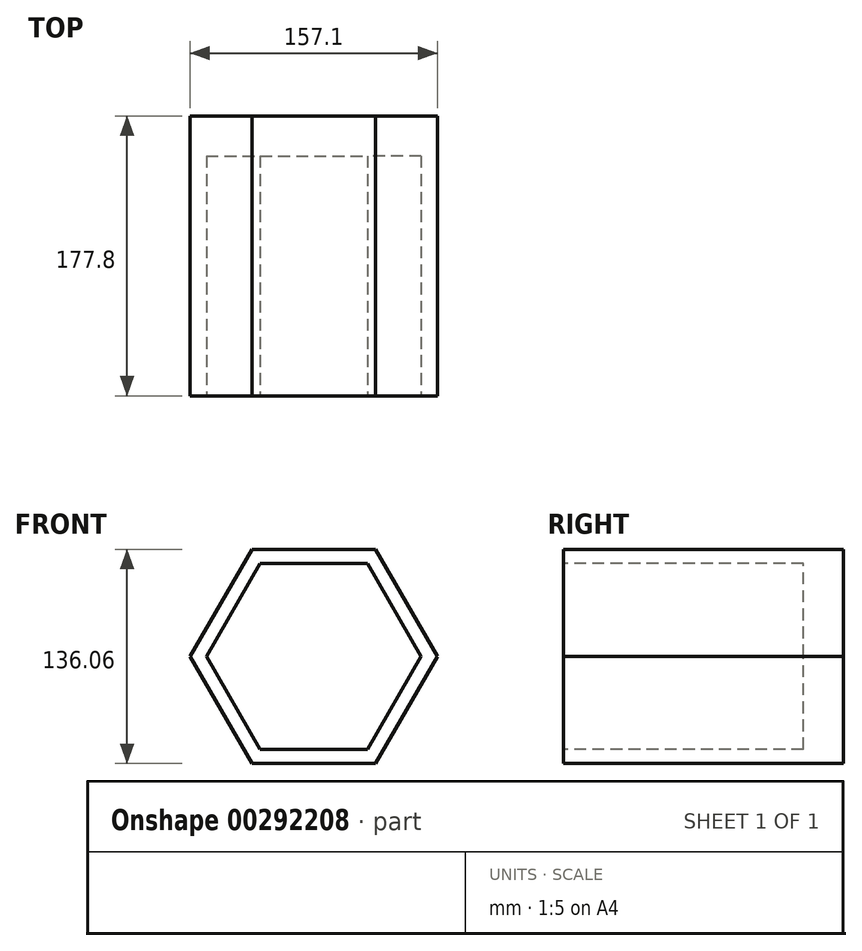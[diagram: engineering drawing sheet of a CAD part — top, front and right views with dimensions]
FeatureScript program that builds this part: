
annotation { "Feature Type Name" : "Feature", "Feature Type Description" : "" }
export const myFeature = defineFeature(function(context is Context, id is Id, definition is map)
    precondition{}
    {
        {
            var Q0;
            Q0=qCreatedBy(makeId("Front.planeOp"),FACE);
            var sketch = newSketch(context, id + "F0", { "sketchPlane" : qUnion([Q0])});
            skCircle(sketch, "E0.cCircle", {"center": v(0, 0) * mm, "radius": 68.03 * mm, "construction": true});
            skLineSegment(sketch, "E0.0", {"start": v(-39.28, 68.03) * mm, "end": v(39.28, 68.03) * mm});
            skLineSegment(sketch, "E0.1", {"start": v(39.28, 68.03) * mm, "end": v(78.55, 0) * mm});
            skLineSegment(sketch, "E0.2", {"start": v(78.55, 0) * mm, "end": v(39.28, -68.03) * mm});
            skLineSegment(sketch, "E0.3", {"start": v(39.28, -68.03) * mm, "end": v(-39.28, -68.03) * mm});
            skLineSegment(sketch, "E0.4", {"start": v(-39.28, -68.03) * mm, "end": v(-78.55, 0) * mm});
            skLineSegment(sketch, "E0.5", {"start": v(-78.55, 0) * mm, "end": v(-39.28, 68.03) * mm});
            skPoint(sketch, "E0.0.midPoint", {"position": v(0, 68.03) * mm});
            skSolve(sketch);
        }
        {
            var Q0;
            Q0 = qSketchRegion(id + "F0", true);
            extrude(context, id + "F1", {"entities" : qUnion([Q0]), "depth" : 177.8 * mm});
        }
        {
            var Q0;
            Q0=makeQuery(id+"F1.opExtrude","CAP_FACE",FACE,{"disambiguationData":[OSD([sQuery(id+"F0.wireOp",EDGE,"E0.0"),sQuery(id+"F0.wireOp",EDGE,"E0.1"),sQuery(id+"F0.wireOp",EDGE,"E0.2"),sQuery(id+"F0.wireOp",EDGE,"E0.3"),sQuery(id+"F0.wireOp",EDGE,"E0.4"),sQuery(id+"F0.wireOp",EDGE,"E0.5")])],"isStart":false});
            var sketch = newSketch(context, id + "F2", { "sketchPlane" : qUnion([Q0])});
            skCircle(sketch, "E1.cCircle", {"center": v(0, 0) * mm, "radius": 59.04 * mm, "construction": true});
            skLineSegment(sketch, "E1.0", {"start": v(-34.09, 59.04) * mm, "end": v(34.09, 59.04) * mm});
            skLineSegment(sketch, "E1.1", {"start": v(34.09, 59.04) * mm, "end": v(68.17, 0) * mm});
            skLineSegment(sketch, "E1.2", {"start": v(68.17, 0) * mm, "end": v(34.09, -59.04) * mm});
            skLineSegment(sketch, "E1.3", {"start": v(34.09, -59.04) * mm, "end": v(-34.09, -59.04) * mm});
            skLineSegment(sketch, "E1.4", {"start": v(-34.09, -59.04) * mm, "end": v(-68.17, 0) * mm});
            skLineSegment(sketch, "E1.5", {"start": v(-68.17, 0) * mm, "end": v(-34.09, 59.04) * mm});
            skPoint(sketch, "E1.0.midPoint", {"position": v(0, 59.04) * mm});
            skSolve(sketch);
        }
        {
            var Q0;
            Q0 = qSketchRegion(id + "F2", true);
            extrude(context, id + "F3", {"entities" : qUnion([Q0]), "operationType" : NewBodyOperationType.REMOVE, "oppositeDirection" : true, "depth" : 152.4 * mm});
        }
    });
